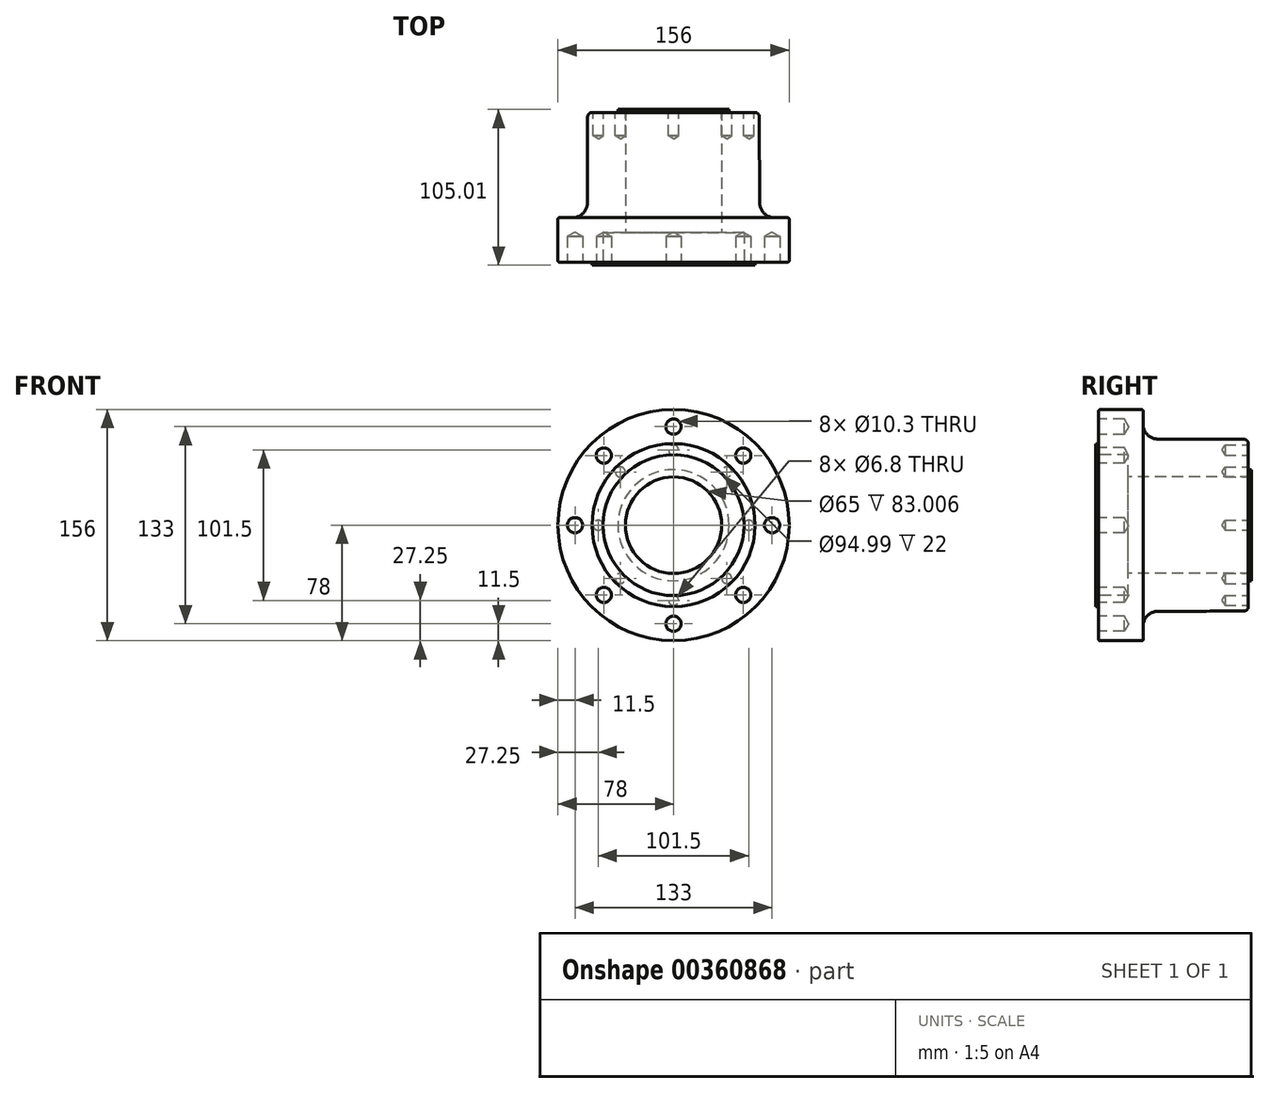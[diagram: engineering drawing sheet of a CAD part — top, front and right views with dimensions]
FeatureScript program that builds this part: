
annotation { "Feature Type Name" : "Feature", "Feature Type Description" : "" }
export const myFeature = defineFeature(function(context is Context, id is Id, definition is map)
    precondition{}
    {
        {
            var Q0;
            Q0=qCreatedBy(makeId("Right.planeOp"),FACE);
            var sketch = newSketch(context, id + "F0", { "sketchPlane" : qUnion([Q0])});
            skLineSegment(sketch, "E0", {"start": v(0, -32.5) * mm, "end": v(0, -37.5) * mm});
            skLineSegment(sketch, "E1", {"start": v(-107, 0) * mm, "end": v(0, 0) * mm});
            skLineSegment(sketch, "E2", {"start": v(0, -37.5) * mm, "end": v(-2, -37.5) * mm});
            skLineSegment(sketch, "E3", {"start": v(-105, -55) * mm, "end": v(-103, -55) * mm});
            skLineSegment(sketch, "E4", {"start": v(-103, -55) * mm, "end": v(-103, -77) * mm});
            skLineSegment(sketch, "E5", {"start": v(-102, -78) * mm, "end": v(-74, -78) * mm});
            skLineSegment(sketch, "E6", {"start": v(-2, -37.5) * mm, "end": v(-2, -54.94) * mm});
            skLineSegment(sketch, "E7", {"start": v(-83, -32.5) * mm, "end": v(-83, -47.5) * mm});
            skLineSegment(sketch, "E8", {"start": v(-83, -47.5) * mm, "end": v(-105, -47.5) * mm});
            skLineSegment(sketch, "E9", {"start": v(-105, -47.5) * mm, "end": v(-105, -55) * mm});
            skLineSegment(sketch, "E10", {"start": v(-151.93, 0) * mm, "end": v(85.07, 0) * mm, "construction": true});
            skLineSegment(sketch, "E11", {"start": v(-73, -77) * mm, "end": v(-73, -68.12) * mm});
            skLineSegment(sketch, "E12", {"start": v(-63.04, -58.12) * mm, "end": v(-5, -57.94) * mm});
            skPoint(sketch, "E13.visualSharp", {"position": v(-73, -58.15) * mm});
            skArc(sketch, "E13.filletArc", {"start": v(-63.04, -58.12) * mm, "mid": v(-70.09, -61.06) * mm, "end": v(-73, -68.12) * mm});
            skLineSegment(sketch, "E14", {"start": v(0, -32.5) * mm, "end": v(-83, -32.5) * mm});
            skPoint(sketch, "E14.endSnap0", {"position": v(-83, -33.12) * mm});
            skPoint(sketch, "E15.visualSharp", {"position": v(-2, -57.93) * mm});
            skArc(sketch, "E15.filletArc", {"start": v(-5, -57.94) * mm, "mid": v(-2.88, -57.06) * mm, "end": v(-2, -54.94) * mm});
            skPoint(sketch, "E16.visualSharp", {"position": v(-73, -78) * mm});
            skArc(sketch, "E16.filletArc", {"start": v(-74, -78) * mm, "mid": v(-73.3, -77.7) * mm, "end": v(-73, -77) * mm});
            skPoint(sketch, "E17.visualSharp", {"position": v(-103, -78) * mm});
            skArc(sketch, "E17.filletArc", {"start": v(-103, -77) * mm, "mid": v(-102.71, -77.7) * mm, "end": v(-102, -78) * mm});
            skSolve(sketch);
        }
        {
            var Q0;
            {var subQ1=sQuery(id+"F0.wireOp",EDGE,"E0");Q0=makeQuery(id+"F0.imprint","IMPRINT",FACE,{"disambiguationData":[TD([[makeQuery(id+"F0.imprint","IMPRINT",EDGE,{"derivedFrom":subQ1}),-1.0]])]});}
            var Q1;
            Q1=sQuery(id+"F0.wireOp",EDGE,"E10");
            revolve(context, id + "F1", {"entities" : qUnion([Q0]), "axis" : qUnion([Q1]), "revolveType" : RevolveType.FULL});
        }
        {
            var Q0;
            Q0=makeQuery(id+"F1.opRevolve","SWEPT_FACE",FACE,{"disambiguationData":[OSD([sQuery(id+"F0.wireOp",EDGE,"E4"),sQuery(id+"F0.wireOp",EDGE,"cfX7JaCO-iJ7T-l7Cb-Mjpo-dRGjAia9Tlp4")])]});
            var sketch = newSketch(context, id + "F2", { "sketchPlane" : qUnion([Q0])});
            skPoint(sketch, "E18", {"position": v(66.5, 0) * mm});
            skPoint(sketch, "E19.1.0", {"position": v(47.02, 47.02) * mm});
            skPoint(sketch, "E19.2.0", {"position": v(0, 66.5) * mm});
            skPoint(sketch, "E19.3.0", {"position": v(-47.02, 47.02) * mm});
            skPoint(sketch, "E19.4.0", {"position": v(-66.5, 0) * mm});
            skPoint(sketch, "E19.5.0", {"position": v(-47.02, -47.02) * mm});
            skPoint(sketch, "E19.6.0", {"position": v(0, -66.5) * mm});
            skPoint(sketch, "E19.7.0", {"position": v(47.02, -47.02) * mm});
            skPoint(sketch, "E19.center", {"position": v(0, 0) * mm});
            skSolve(sketch);
        }
        {
            var Q0;
            Q0=sQuery(id+"F2.wireOp",VERTEX,"E19.2.0");
            var Q1;
            Q1=sQuery(id+"F2.wireOp",VERTEX,"E19.1.0");
            var Q2;
            Q2=sQuery(id+"F2.wireOp",VERTEX,"E18");
            var Q3;
            Q3=sQuery(id+"F2.wireOp",VERTEX,"E19.7.0");
            var Q4;
            Q4=sQuery(id+"F2.wireOp",VERTEX,"E19.6.0");
            var Q5;
            Q5=sQuery(id+"F2.wireOp",VERTEX,"E19.5.0");
            var Q6;
            Q6=sQuery(id+"F2.wireOp",VERTEX,"E19.4.0");
            var Q7;
            Q7=sQuery(id+"F2.wireOp",VERTEX,"E19.3.0");
            var Q8;
            Q8=makeQuery(id+"F1.opRevolve","SWEPT_BODY",BODY,{"disambiguationData":[OSD([sQuery(id+"F0.wireOp",EDGE,"E0"),sQuery(id+"F0.wireOp",EDGE,"E1"),sQuery(id+"F0.wireOp",EDGE,"E2"),sQuery(id+"F0.wireOp",EDGE,"E3"),sQuery(id+"F0.wireOp",EDGE,"E4"),sQuery(id+"F0.wireOp",EDGE,"E5"),sQuery(id+"F0.wireOp",EDGE,"E6"),sQuery(id+"F0.wireOp",EDGE,"y0hNy5Yb-BOWU-prQD-YGgL-2uF1fygJb49L"),sQuery(id+"F0.wireOp",EDGE,"iOVRLZjb-FgfH-Qglw-dNpz-AlPQz6SV3xSw"),sQuery(id+"F0.wireOp",EDGE,"E7"),sQuery(id+"F0.wireOp",EDGE,"E8"),sQuery(id+"F0.wireOp",EDGE,"E9"),sQuery(id+"F0.wireOp",EDGE,"cfX7JaCO-iJ7T-l7Cb-Mjpo-dRGjAia9Tlp4")])]});
            hole(context, id + "F3", {"style" : HoleStyle.SIMPLE, "endStyle" : HoleEndStyle.BLIND, "standardTappedOrClearance" : lookupTablePath({ "standard" : "ISO", "engagement" : "75%", "pitch" : "1.75 mm", "size" : "M12", "type" : "Tapped" }), "standardBlindInLast" : lookupTablePath({ "standard" : "ISO", "engagement" : "75%", "pitch" : "1.75 mm", "size" : "M12", "type" : "Tapped" }), "holeDiameter" : 10.3 * mm, "showTappedDepth" : true, "holeDepth" : 17.25 * mm, "isTappedThrough" : true, "tappedDepth" : 12 * mm, "tapClearance" : 3, "startFromSketch" : true, "locations" : qUnion([Q0, Q1, Q2, Q3, Q4, Q5, Q6, Q7]), "scope" : qUnion([Q8]), "majorDiameter" : 12 * mm});
        }
        {
            var Q0;
            Q0=makeQuery(id+"F1.opRevolve","SWEPT_FACE",FACE,{"disambiguationData":[OSD([sQuery(id+"F0.wireOp",EDGE,"E6")])]});
            var sketch = newSketch(context, id + "F4", { "sketchPlane" : qUnion([Q0])});
            skPoint(sketch, "E20", {"position": v(0, 50.75) * mm});
            skPoint(sketch, "E21.1.0", {"position": v(-35.89, 35.89) * mm});
            skPoint(sketch, "E21.2.0", {"position": v(-50.75, 0) * mm});
            skPoint(sketch, "E21.3.0", {"position": v(-35.89, -35.89) * mm});
            skPoint(sketch, "E21.4.0", {"position": v(0, -50.75) * mm});
            skPoint(sketch, "E21.5.0", {"position": v(35.89, -35.89) * mm});
            skPoint(sketch, "E21.6.0", {"position": v(50.75, 0) * mm});
            skPoint(sketch, "E21.7.0", {"position": v(35.89, 35.89) * mm});
            skPoint(sketch, "E21.center", {"position": v(0, 0) * mm});
            skSolve(sketch);
        }
        {
            var Q0;
            Q0=sQuery(id+"F4.wireOp",VERTEX,"E20");
            var Q1;
            Q1=sQuery(id+"F4.wireOp",VERTEX,"E21.7.0");
            var Q2;
            Q2=sQuery(id+"F4.wireOp",VERTEX,"E21.6.0");
            var Q3;
            Q3=sQuery(id+"F4.wireOp",VERTEX,"E21.5.0");
            var Q4;
            Q4=sQuery(id+"F4.wireOp",VERTEX,"E21.4.0");
            var Q5;
            Q5=sQuery(id+"F4.wireOp",VERTEX,"E21.3.0");
            var Q6;
            Q6=sQuery(id+"F4.wireOp",VERTEX,"E21.2.0");
            var Q7;
            Q7=sQuery(id+"F4.wireOp",VERTEX,"E21.1.0");
            var Q8;
            Q8=makeQuery(id+"F1.opRevolve","SWEPT_BODY",BODY,{"disambiguationData":[OSD([sQuery(id+"F0.wireOp",EDGE,"E0"),sQuery(id+"F0.wireOp",EDGE,"E1"),sQuery(id+"F0.wireOp",EDGE,"E2"),sQuery(id+"F0.wireOp",EDGE,"E3"),sQuery(id+"F0.wireOp",EDGE,"E4"),sQuery(id+"F0.wireOp",EDGE,"E5"),sQuery(id+"F0.wireOp",EDGE,"E6"),sQuery(id+"F0.wireOp",EDGE,"y0hNy5Yb-BOWU-prQD-YGgL-2uF1fygJb49L"),sQuery(id+"F0.wireOp",EDGE,"iOVRLZjb-FgfH-Qglw-dNpz-AlPQz6SV3xSw"),sQuery(id+"F0.wireOp",EDGE,"E7"),sQuery(id+"F0.wireOp",EDGE,"E8"),sQuery(id+"F0.wireOp",EDGE,"E9"),sQuery(id+"F0.wireOp",EDGE,"cfX7JaCO-iJ7T-l7Cb-Mjpo-dRGjAia9Tlp4")])]});
            hole(context, id + "F5", {"style" : HoleStyle.SIMPLE, "endStyle" : HoleEndStyle.BLIND, "standardTappedOrClearance" : lookupTablePath({ "standard" : "ISO", "engagement" : "75%", "pitch" : "1.25 mm", "size" : "M8", "type" : "Tapped" }), "standardBlindInLast" : lookupTablePath({ "standard" : "ISO", "engagement" : "75%", "pitch" : "1.25 mm", "size" : "M8", "type" : "Tapped" }), "holeDiameter" : 6.8 * mm, "showTappedDepth" : true, "holeDepth" : 15.75 * mm, "isTappedThrough" : true, "tappedDepth" : 12 * mm, "tapClearance" : 3, "startFromSketch" : true, "locations" : qUnion([Q0, Q1, Q2, Q3, Q4, Q5, Q6, Q7]), "scope" : qUnion([Q8]), "majorDiameter" : 8 * mm});
        }
    });
